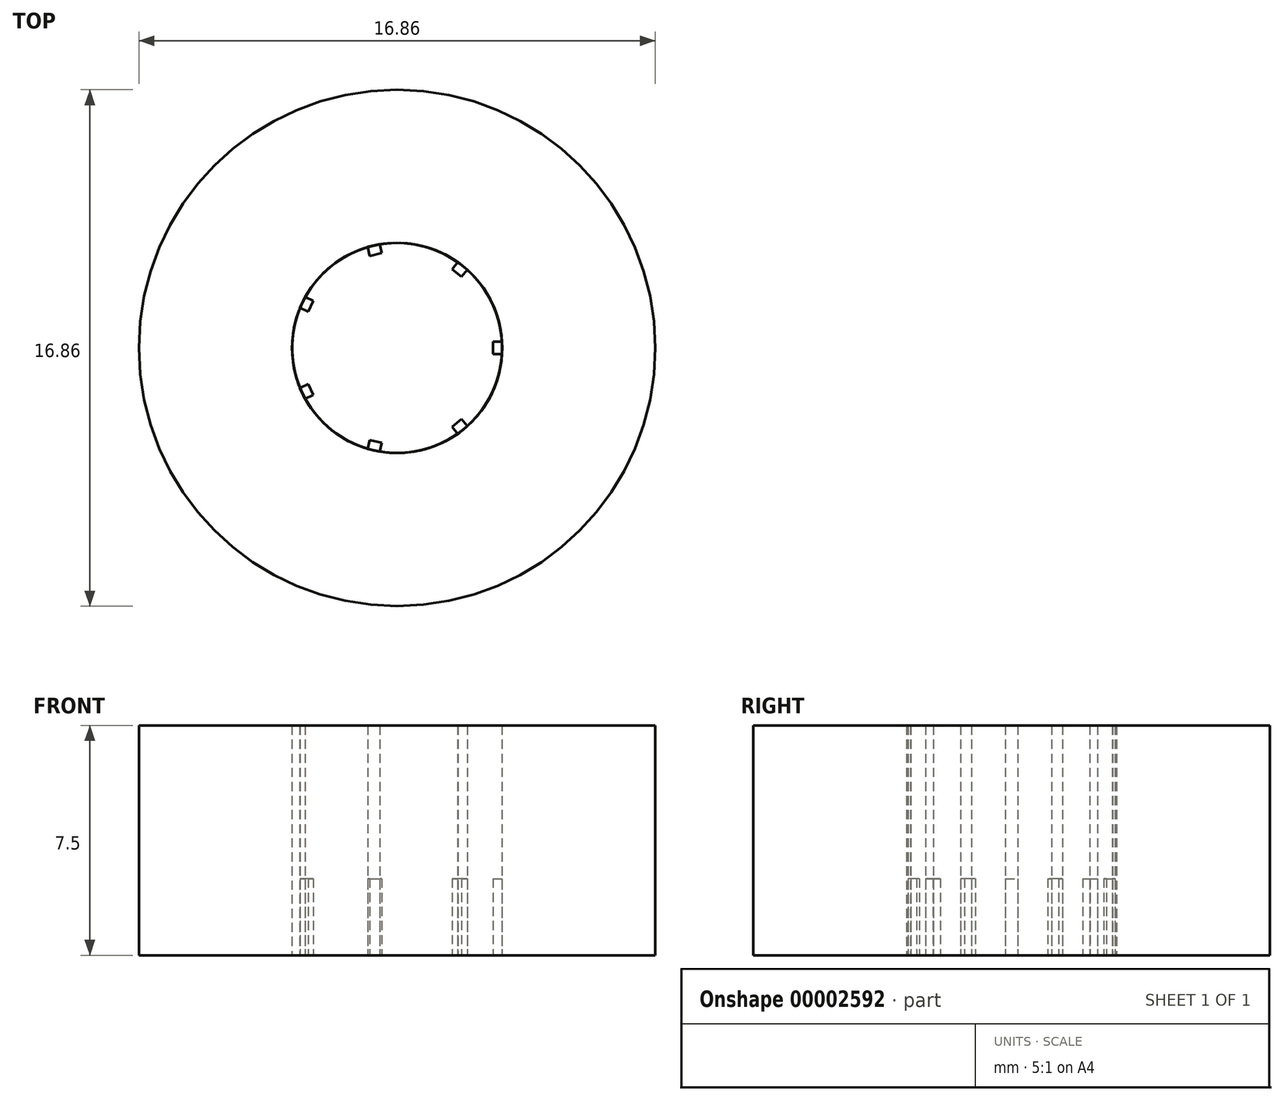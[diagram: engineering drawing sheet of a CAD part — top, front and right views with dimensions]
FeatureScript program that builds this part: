
annotation { "Feature Type Name" : "Feature", "Feature Type Description" : "" }
export const myFeature = defineFeature(function(context is Context, id is Id, definition is map)
    precondition{}
    {
        {
            var Q0;
            Q0=qCreatedBy(makeId("Top.planeOp"),FACE);
            var sketch = newSketch(context, id + "F0", { "sketchPlane" : qUnion([Q0])});
            skCircle(sketch, "E0", {"center": v(0, 0) * mm, "radius": 3.43 * mm});
            skCircle(sketch, "E1.0", {"center": v(0, 0) * mm, "radius": 8.43 * mm});
            skLineSegment(sketch, "E2.bottom", {"start": v(3.13, -0.2) * mm, "end": v(3.43, -0.2) * mm});
            skLineSegment(sketch, "E2.top", {"start": v(3.13, 0.2) * mm, "end": v(3.43, 0.2) * mm});
            skLineSegment(sketch, "E2.left", {"start": v(3.13, -0.2) * mm, "end": v(3.13, 0.2) * mm});
            skLineSegment(sketch, "E2.right", {"start": v(3.43, -0.2) * mm, "end": v(3.43, 0.2) * mm});
            skLineSegment(sketch, "E3", {"start": v(0, 0) * mm, "end": v(3.43, 0) * mm, "construction": true});
            skLineSegment(sketch, "E4", {"start": v(3.22, 0.2) * mm, "end": v(3.43, 0.2) * mm, "construction": true});
            skLineSegment(sketch, "E5", {"start": v(3.22, 0.2) * mm, "end": v(3.22, 0) * mm, "construction": true});
            skLineSegment(sketch, "E6", {"start": v(3.22, 0) * mm, "end": v(3.22, -0.2) * mm, "construction": true});
            skSolve(sketch);
        }
        {
            var Q0;
            Q0=makeQuery(id+"F0.imprint","IMPRINT",FACE,{"disambiguationData":[TD([[makeQuery(id+"F0.imprint","IMPRINT",EDGE,{"derivedFrom":sQuery(id+"F0.wireOp",EDGE,"E1.0")}),1.0]])]});
            extrude(context, id + "F1", {"entities" : qUnion([Q0]), "depth" : 5 * mm});
        }
        {
            var Q0;
            {var subQ0=sQuery(id+"F0.wireOp",EDGE,"E2.left");Q0=makeQuery(id+"F0.imprint","IMPRINT",FACE,{"disambiguationData":[TD([[makeQuery(id+"F0.imprint","IMPRINT",EDGE,{"derivedFrom":subQ0}),-1.0]])]});}
            var Q1;
            Q1=makeQuery(id+"F1.opExtrude","CAP_FACE",FACE,{"disambiguationData":[OSD([sQuery(id+"F0.wireOp",EDGE,"E0"),sQuery(id+"F0.wireOp",EDGE,"E1.0"),sQuery(id+"F0.wireOp",EDGE,"E2.bottom"),sQuery(id+"F0.wireOp",EDGE,"E2.top"),sQuery(id+"F0.wireOp",EDGE,"E2.right")])],"isStart":false});
            extrude(context, id + "F2", {"entities" : qUnion([Q0, Q1]), "operationType" : NewBodyOperationType.ADD, "depth" : 2.5 * mm});
        }
        {
            var Q0;
            {var subQ0=sQuery(id+"F0.wireOp",EDGE,"E0");var subQ1=sQuery(id+"F0.wireOp",EDGE,"E2.bottom");var subQ2=sQuery(id+"F0.wireOp",EDGE,"E2.top");Q0=makeQuery(id+"F2.boolean.opBoolean","MERGE",BODY,{"derivedFrom":[makeQuery(id+"F1.opExtrude","SWEPT_BODY",BODY,{"disambiguationData":[OSD([subQ0,sQuery(id+"F0.wireOp",EDGE,"E1.0"),subQ1,subQ2,sQuery(id+"F0.wireOp",EDGE,"E2.right")])]}),makeQuery(id+"F2.opExtrude","SWEPT_BODY",BODY,{"disambiguationData":[OSD([subQ0,subQ1,subQ2,sQuery(id+"F0.wireOp",EDGE,"E2.left")])]})]});}
            var Q1;
            Q1=makeQuery(id+"F1.opExtrude","CAP_EDGE",EDGE,{"disambiguationData":[OSD([sQuery(id+"F0.wireOp",EDGE,"E0")])],"isStart":true});
            circularPattern(context, id + "F3", {"entities" : qUnion([Q0]), "axis" : qUnion([Q1]), "angle" : 360 * degree, "instanceCount" : 7, "equalSpace" : true});
        }
    });
